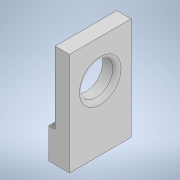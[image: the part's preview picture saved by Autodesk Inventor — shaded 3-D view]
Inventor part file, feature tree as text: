
AUTODESK INVENTOR PART (.ipt)
format: ipt  version: 2022 (Build 260153000, 153)  size: 137,216 bytes
history: native  units: mm
features: extrude x4, sketch x4, fillet x1
ambient origin geometry x8: Origin, YZ Plane, XZ Plane, XY Plane, X Axis, Y Axis, Z Axis, Center Point
bodies: Solid1 (feature_tree)
feature tree (9):
  extrude  "Extrusion1"  Depth=30.0mm
  extrude  "Extrusion2"  Depth=3.0mm
  extrude  "Extrusion3"  Depth=50.0mm
  fillet  "Fillet1"  Radius=50.0mm
  extrude  "Extrusion4"  Depth=3.0mm TaperAngle=0.0deg
  sketch  "Sketch1"  dims[d0=10.0mm d1=30.0mm]
  sketch  "Sketch2"  dims[d2=50.0mm d3=0.0mm d7=3.0mm]
  sketch  "Sketch3"  dims[d8=8.0mm d9=0.0mm d11=16.25mm d12=50.0mm d13=0.0mm]
  sketch  "Sketch4"  dims[d14=2.0mm d15=3.0mm d16=0.0mm]
